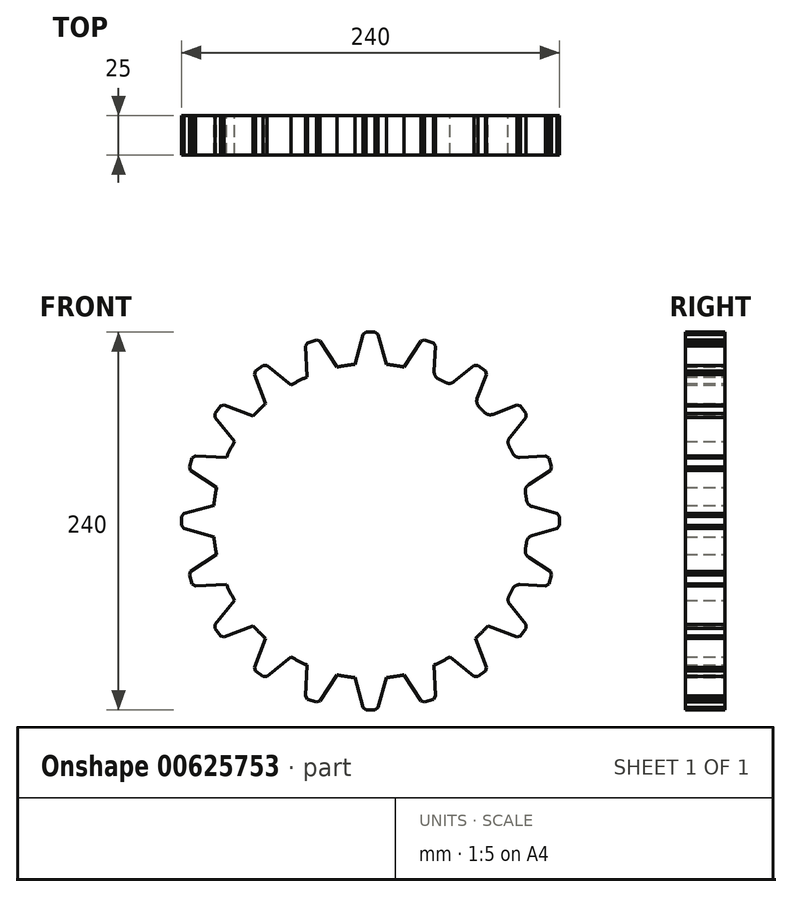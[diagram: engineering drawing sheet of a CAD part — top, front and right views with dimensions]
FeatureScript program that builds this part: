
annotation { "Feature Type Name" : "Feature", "Feature Type Description" : "" }
export const myFeature = defineFeature(function(context is Context, id is Id, definition is map)
    precondition{}
    {
        {
            var Q0;
            Q0=qCreatedBy(makeId("Front.planeOp"),FACE);
            var sketch = newSketch(context, id + "F0", { "sketchPlane" : qUnion([Q0])});
            skArc(sketch, "E0", {"start": v(-40.25, 91.54) * mm, "mid": v(-45.4, 89.1) * mm, "end": v(-50.4, 86.37) * mm});
            skCircle(sketch, "E1", {"center": v(0, 0) * mm, "radius": 120 * mm, "construction": true});
            skLineSegment(sketch, "E2", {"start": v(0, 120) * mm, "end": v(-4.5, 120) * mm});
            skLineSegment(sketch, "E3", {"start": v(0, 120) * mm, "end": v(4.5, 120) * mm});
            skLineSegment(sketch, "E4", {"start": v(4.5, 120) * mm, "end": v(10, 99.5) * mm});
            skLineSegment(sketch, "E5", {"start": v(-4.5, 120) * mm, "end": v(-10, 99.5) * mm});
            skLineSegment(sketch, "E6.1.0", {"start": v(-37.08, 114.13) * mm, "end": v(-32.8, 115.52) * mm});
            skLineSegment(sketch, "E6.1.1", {"start": v(-37.08, 114.13) * mm, "end": v(-41.36, 112.74) * mm});
            skLineSegment(sketch, "E6.1.2", {"start": v(-32.8, 115.52) * mm, "end": v(-21.24, 97.72) * mm});
            skLineSegment(sketch, "E6.1.3", {"start": v(-41.36, 112.74) * mm, "end": v(-40.25, 91.54) * mm});
            skLineSegment(sketch, "E6.2.0", {"start": v(-70.53, 97.08) * mm, "end": v(-66.9, 99.73) * mm});
            skLineSegment(sketch, "E6.2.1", {"start": v(-70.53, 97.08) * mm, "end": v(-74.17, 94.44) * mm});
            skLineSegment(sketch, "E6.2.2", {"start": v(-66.9, 99.73) * mm, "end": v(-50.4, 86.37) * mm});
            skLineSegment(sketch, "E6.2.3", {"start": v(-74.17, 94.44) * mm, "end": v(-66.57, 74.62) * mm});
            skLineSegment(sketch, "E7.3.3.0", {"start": v(-97.08, 70.53) * mm, "end": v(-99.73, 66.9) * mm});
            skLineSegment(sketch, "E7.6.3.0", {"start": v(-94.44, 74.17) * mm, "end": v(-74.62, 66.57) * mm});
            skLineSegment(sketch, "E7.9.3.0", {"start": v(-99.73, 66.9) * mm, "end": v(-86.37, 50.4) * mm});
            skLineSegment(sketch, "E7.11.3.0", {"start": v(-97.08, 70.53) * mm, "end": v(-94.44, 74.17) * mm});
            skLineSegment(sketch, "E7.3.4.0", {"start": v(-114.13, 37.08) * mm, "end": v(-115.52, 32.8) * mm});
            skLineSegment(sketch, "E7.6.4.0", {"start": v(-112.74, 41.36) * mm, "end": v(-91.54, 40.25) * mm});
            skLineSegment(sketch, "E7.9.4.0", {"start": v(-115.52, 32.8) * mm, "end": v(-97.72, 21.24) * mm});
            skLineSegment(sketch, "E7.11.4.0", {"start": v(-114.13, 37.08) * mm, "end": v(-112.74, 41.36) * mm});
            skLineSegment(sketch, "E7.3.5.0", {"start": v(-120, 0) * mm, "end": v(-120, -4.5) * mm});
            skLineSegment(sketch, "E7.6.5.0", {"start": v(-120, 4.5) * mm, "end": v(-99.5, 10) * mm});
            skLineSegment(sketch, "E7.9.5.0", {"start": v(-120, -4.5) * mm, "end": v(-99.5, -10) * mm});
            skLineSegment(sketch, "E7.11.5.0", {"start": v(-120, 0) * mm, "end": v(-120, 4.5) * mm});
            skLineSegment(sketch, "E7.3.6.0", {"start": v(-114.13, -37.08) * mm, "end": v(-112.74, -41.36) * mm});
            skLineSegment(sketch, "E7.6.6.0", {"start": v(-115.52, -32.8) * mm, "end": v(-97.72, -21.24) * mm});
            skLineSegment(sketch, "E7.9.6.0", {"start": v(-112.74, -41.36) * mm, "end": v(-91.54, -40.25) * mm});
            skLineSegment(sketch, "E7.11.6.0", {"start": v(-114.13, -37.08) * mm, "end": v(-115.52, -32.8) * mm});
            skLineSegment(sketch, "E7.3.7.0", {"start": v(-97.08, -70.53) * mm, "end": v(-94.44, -74.17) * mm});
            skLineSegment(sketch, "E7.6.7.0", {"start": v(-99.73, -66.9) * mm, "end": v(-86.37, -50.4) * mm});
            skLineSegment(sketch, "E7.9.7.0", {"start": v(-94.44, -74.17) * mm, "end": v(-74.62, -66.57) * mm});
            skLineSegment(sketch, "E7.11.7.0", {"start": v(-97.08, -70.53) * mm, "end": v(-99.73, -66.9) * mm});
            skLineSegment(sketch, "E7.3.8.0", {"start": v(-70.53, -97.08) * mm, "end": v(-66.9, -99.73) * mm});
            skLineSegment(sketch, "E7.6.8.0", {"start": v(-74.17, -94.44) * mm, "end": v(-66.57, -74.62) * mm});
            skLineSegment(sketch, "E7.9.8.0", {"start": v(-66.9, -99.73) * mm, "end": v(-50.4, -86.37) * mm});
            skLineSegment(sketch, "E7.11.8.0", {"start": v(-70.53, -97.08) * mm, "end": v(-74.17, -94.44) * mm});
            skLineSegment(sketch, "E7.3.9.0", {"start": v(-37.08, -114.13) * mm, "end": v(-32.8, -115.52) * mm});
            skLineSegment(sketch, "E7.6.9.0", {"start": v(-41.36, -112.74) * mm, "end": v(-40.25, -91.54) * mm});
            skLineSegment(sketch, "E7.9.9.0", {"start": v(-32.8, -115.52) * mm, "end": v(-21.24, -97.72) * mm});
            skLineSegment(sketch, "E7.11.9.0", {"start": v(-37.08, -114.13) * mm, "end": v(-41.36, -112.74) * mm});
            skLineSegment(sketch, "E7.3.10.0", {"start": v(0, -120) * mm, "end": v(4.5, -120) * mm});
            skLineSegment(sketch, "E7.6.10.0", {"start": v(-4.5, -120) * mm, "end": v(-10, -99.5) * mm});
            skLineSegment(sketch, "E7.9.10.0", {"start": v(4.5, -120) * mm, "end": v(10, -99.5) * mm});
            skLineSegment(sketch, "E7.11.10.0", {"start": v(0, -120) * mm, "end": v(-4.5, -120) * mm});
            skLineSegment(sketch, "E7.3.11.0", {"start": v(37.08, -114.13) * mm, "end": v(41.36, -112.74) * mm});
            skLineSegment(sketch, "E7.6.11.0", {"start": v(32.8, -115.52) * mm, "end": v(21.24, -97.72) * mm});
            skLineSegment(sketch, "E7.9.11.0", {"start": v(41.36, -112.74) * mm, "end": v(40.25, -91.54) * mm});
            skLineSegment(sketch, "E7.11.11.0", {"start": v(37.08, -114.13) * mm, "end": v(32.8, -115.52) * mm});
            skLineSegment(sketch, "E7.3.12.0", {"start": v(70.53, -97.08) * mm, "end": v(74.17, -94.44) * mm});
            skLineSegment(sketch, "E7.6.12.0", {"start": v(66.9, -99.73) * mm, "end": v(50.4, -86.37) * mm});
            skLineSegment(sketch, "E7.9.12.0", {"start": v(74.17, -94.44) * mm, "end": v(66.57, -74.62) * mm});
            skLineSegment(sketch, "E7.11.12.0", {"start": v(70.53, -97.08) * mm, "end": v(66.9, -99.73) * mm});
            skLineSegment(sketch, "E7.3.13.0", {"start": v(97.08, -70.53) * mm, "end": v(99.73, -66.9) * mm});
            skLineSegment(sketch, "E7.6.13.0", {"start": v(94.44, -74.17) * mm, "end": v(74.62, -66.57) * mm});
            skLineSegment(sketch, "E7.9.13.0", {"start": v(99.73, -66.9) * mm, "end": v(86.37, -50.4) * mm});
            skLineSegment(sketch, "E7.11.13.0", {"start": v(97.08, -70.53) * mm, "end": v(94.44, -74.17) * mm});
            skLineSegment(sketch, "E7.3.14.0", {"start": v(114.13, -37.08) * mm, "end": v(115.52, -32.8) * mm});
            skLineSegment(sketch, "E7.6.14.0", {"start": v(112.74, -41.36) * mm, "end": v(91.54, -40.25) * mm});
            skLineSegment(sketch, "E7.9.14.0", {"start": v(115.52, -32.8) * mm, "end": v(97.72, -21.24) * mm});
            skLineSegment(sketch, "E7.11.14.0", {"start": v(114.13, -37.08) * mm, "end": v(112.74, -41.36) * mm});
            skLineSegment(sketch, "E7.3.15.0", {"start": v(120, 0) * mm, "end": v(120, 4.5) * mm});
            skLineSegment(sketch, "E7.6.15.0", {"start": v(120, -4.5) * mm, "end": v(99.5, -10) * mm});
            skLineSegment(sketch, "E7.9.15.0", {"start": v(120, 4.5) * mm, "end": v(99.5, 10) * mm});
            skLineSegment(sketch, "E7.11.15.0", {"start": v(120, 0) * mm, "end": v(120, -4.5) * mm});
            skLineSegment(sketch, "E7.3.16.0", {"start": v(114.13, 37.08) * mm, "end": v(112.74, 41.36) * mm});
            skLineSegment(sketch, "E7.6.16.0", {"start": v(115.52, 32.8) * mm, "end": v(97.72, 21.24) * mm});
            skLineSegment(sketch, "E7.9.16.0", {"start": v(112.74, 41.36) * mm, "end": v(91.54, 40.25) * mm});
            skLineSegment(sketch, "E7.11.16.0", {"start": v(114.13, 37.08) * mm, "end": v(115.52, 32.8) * mm});
            skLineSegment(sketch, "E7.3.17.0", {"start": v(97.08, 70.53) * mm, "end": v(94.44, 74.17) * mm});
            skLineSegment(sketch, "E7.6.17.0", {"start": v(99.73, 66.9) * mm, "end": v(86.37, 50.4) * mm});
            skLineSegment(sketch, "E7.9.17.0", {"start": v(94.44, 74.17) * mm, "end": v(74.62, 66.57) * mm});
            skLineSegment(sketch, "E7.11.17.0", {"start": v(97.08, 70.53) * mm, "end": v(99.73, 66.9) * mm});
            skLineSegment(sketch, "E7.3.18.0", {"start": v(70.53, 97.08) * mm, "end": v(66.9, 99.73) * mm});
            skLineSegment(sketch, "E7.6.18.0", {"start": v(74.17, 94.44) * mm, "end": v(66.57, 74.62) * mm});
            skLineSegment(sketch, "E7.9.18.0", {"start": v(66.9, 99.73) * mm, "end": v(50.4, 86.37) * mm});
            skLineSegment(sketch, "E7.11.18.0", {"start": v(70.53, 97.08) * mm, "end": v(74.17, 94.44) * mm});
            skLineSegment(sketch, "E7.3.19.0", {"start": v(37.08, 114.13) * mm, "end": v(32.8, 115.52) * mm});
            skLineSegment(sketch, "E7.6.19.0", {"start": v(41.36, 112.74) * mm, "end": v(40.25, 91.54) * mm});
            skLineSegment(sketch, "E7.9.19.0", {"start": v(32.8, 115.52) * mm, "end": v(21.24, 97.72) * mm});
            skLineSegment(sketch, "E7.11.19.0", {"start": v(37.08, 114.13) * mm, "end": v(41.36, 112.74) * mm});
            skArc(sketch, "E8.trimOffspring", {"start": v(-10, 99.5) * mm, "mid": v(-15.64, 98.77) * mm, "end": v(-21.24, 97.72) * mm});
            skArc(sketch, "E9.trimOffspring", {"start": v(21.24, 97.72) * mm, "mid": v(15.64, 98.77) * mm, "end": v(10, 99.5) * mm});
            skArc(sketch, "E10.trimOffspring", {"start": v(50.4, 86.37) * mm, "mid": v(45.4, 89.1) * mm, "end": v(40.25, 91.54) * mm});
            skArc(sketch, "E11.trimOffspring", {"start": v(74.62, 66.57) * mm, "mid": v(70.71, 70.71) * mm, "end": v(66.57, 74.62) * mm});
            skArc(sketch, "E12.trimOffspring", {"start": v(91.54, 40.25) * mm, "mid": v(89.1, 45.4) * mm, "end": v(86.37, 50.4) * mm});
            skArc(sketch, "E13.trimOffspring", {"start": v(99.5, 10) * mm, "mid": v(98.77, 15.64) * mm, "end": v(97.72, 21.24) * mm});
            skArc(sketch, "E14.trimOffspring", {"start": v(97.72, -21.24) * mm, "mid": v(98.77, -15.64) * mm, "end": v(99.5, -10) * mm});
            skArc(sketch, "E15.trimOffspring", {"start": v(86.37, -50.4) * mm, "mid": v(89.1, -45.4) * mm, "end": v(91.54, -40.25) * mm});
            skArc(sketch, "E16.trimOffspring", {"start": v(66.57, -74.62) * mm, "mid": v(70.71, -70.71) * mm, "end": v(74.62, -66.57) * mm});
            skArc(sketch, "E17.trimOffspring", {"start": v(40.25, -91.54) * mm, "mid": v(45.4, -89.1) * mm, "end": v(50.4, -86.37) * mm});
            skArc(sketch, "E18.trimOffspring", {"start": v(10, -99.5) * mm, "mid": v(15.64, -98.77) * mm, "end": v(21.24, -97.72) * mm});
            skArc(sketch, "E19.trimOffspring", {"start": v(-21.24, -97.72) * mm, "mid": v(-15.64, -98.77) * mm, "end": v(-10, -99.5) * mm});
            skArc(sketch, "E20.trimOffspring", {"start": v(-50.4, -86.37) * mm, "mid": v(-45.4, -89.1) * mm, "end": v(-40.25, -91.54) * mm});
            skArc(sketch, "E21.trimOffspring", {"start": v(-74.62, -66.57) * mm, "mid": v(-70.71, -70.71) * mm, "end": v(-66.57, -74.62) * mm});
            skArc(sketch, "E22.trimOffspring", {"start": v(-91.54, -40.25) * mm, "mid": v(-89.1, -45.4) * mm, "end": v(-86.37, -50.4) * mm});
            skArc(sketch, "E23.trimOffspring", {"start": v(-99.5, -10) * mm, "mid": v(-98.77, -15.64) * mm, "end": v(-97.72, -21.24) * mm});
            skArc(sketch, "E24.trimOffspring", {"start": v(-97.72, 21.24) * mm, "mid": v(-98.77, 15.64) * mm, "end": v(-99.5, 10) * mm});
            skArc(sketch, "E25.trimOffspring", {"start": v(-86.37, 50.4) * mm, "mid": v(-89.1, 45.4) * mm, "end": v(-91.54, 40.25) * mm});
            skArc(sketch, "E26.trimOffspring", {"start": v(-66.57, 74.62) * mm, "mid": v(-70.71, 70.71) * mm, "end": v(-74.62, 66.57) * mm});
            skSolve(sketch);
        }
        {
            var Q0;
            Q0=makeQuery(id+"F0.imprint","IMPRINT",FACE,{"disambiguationData":[TD([[makeQuery(id+"F0.imprint","IMPRINT",EDGE,{"derivedFrom":sQuery(id+"F0.wireOp",EDGE,"E0")}),1.0]])]});
            extrude(context, id + "F1", {"entities" : qUnion([Q0]), "endBound" : BoundingType.SYMMETRIC, "depth" : 25 * mm, "offsetDistance" : 25 * mm});
        }
        {
            var Q0;
            Q0=makeQuery(id+"F1.opExtrude","SWEPT_EDGE",EDGE,{"disambiguationData":[OSD([sQuery(id+"F0.wireOp",EDGE,"E7.6.19.0"),sQuery(id+"F0.wireOp",EDGE,"E10.trimOffspring")])]});
            var Q1;
            Q1=makeQuery(id+"F1.opExtrude","SWEPT_EDGE",EDGE,{"disambiguationData":[OSD([sQuery(id+"F0.wireOp",EDGE,"E7.9.18.0"),sQuery(id+"F0.wireOp",EDGE,"E10.trimOffspring")])]});
            fillet(context, id + "F2", {"entities" : qUnion([Q0, Q1]), "radius" : 5 * mm, "tangentPropagation" : true, "allowEdgeOverflow" : false});
        }
        {
            var Q0;
            Q0=makeQuery(id+"F1.opExtrude","SWEPT_EDGE",EDGE,{"disambiguationData":[OSD([sQuery(id+"F0.wireOp",EDGE,"E6.2.0"),sQuery(id+"F0.wireOp",EDGE,"E6.2.2")])]});
            var Q1;
            Q1=makeQuery(id+"F1.opExtrude","SWEPT_EDGE",EDGE,{"disambiguationData":[OSD([sQuery(id+"F0.wireOp",EDGE,"E6.2.1"),sQuery(id+"F0.wireOp",EDGE,"E6.2.3")])]});
            var Q2;
            Q2=makeQuery(id+"F1.opExtrude","SWEPT_EDGE",EDGE,{"disambiguationData":[OSD([sQuery(id+"F0.wireOp",EDGE,"E6.1.0"),sQuery(id+"F0.wireOp",EDGE,"E6.1.2")])]});
            var Q3;
            Q3=makeQuery(id+"F1.opExtrude","SWEPT_EDGE",EDGE,{"disambiguationData":[OSD([sQuery(id+"F0.wireOp",EDGE,"E6.1.1"),sQuery(id+"F0.wireOp",EDGE,"E6.1.3")])]});
            var Q4;
            Q4=makeQuery(id+"F1.opExtrude","SWEPT_EDGE",EDGE,{"disambiguationData":[OSD([sQuery(id+"F0.wireOp",EDGE,"E3"),sQuery(id+"F0.wireOp",EDGE,"E4")])]});
            var Q5;
            Q5=makeQuery(id+"F1.opExtrude","SWEPT_EDGE",EDGE,{"disambiguationData":[OSD([sQuery(id+"F0.wireOp",EDGE,"E2"),sQuery(id+"F0.wireOp",EDGE,"E5")])]});
            var Q6;
            Q6=makeQuery(id+"F1.opExtrude","SWEPT_EDGE",EDGE,{"disambiguationData":[OSD([sQuery(id+"F0.wireOp",EDGE,"E7.6.19.0"),sQuery(id+"F0.wireOp",EDGE,"E7.11.19.0")])]});
            var Q7;
            Q7=makeQuery(id+"F1.opExtrude","SWEPT_EDGE",EDGE,{"disambiguationData":[OSD([sQuery(id+"F0.wireOp",EDGE,"E7.3.19.0"),sQuery(id+"F0.wireOp",EDGE,"E7.9.19.0")])]});
            var Q8;
            Q8=makeQuery(id+"F1.opExtrude","SWEPT_EDGE",EDGE,{"disambiguationData":[OSD([sQuery(id+"F0.wireOp",EDGE,"E7.6.18.0"),sQuery(id+"F0.wireOp",EDGE,"E7.11.18.0")])]});
            var Q9;
            Q9=makeQuery(id+"F1.opExtrude","SWEPT_EDGE",EDGE,{"disambiguationData":[OSD([sQuery(id+"F0.wireOp",EDGE,"E7.3.18.0"),sQuery(id+"F0.wireOp",EDGE,"E7.9.18.0")])]});
            var Q10;
            Q10=makeQuery(id+"F1.opExtrude","SWEPT_EDGE",EDGE,{"disambiguationData":[OSD([sQuery(id+"F0.wireOp",EDGE,"E7.6.17.0"),sQuery(id+"F0.wireOp",EDGE,"E7.11.17.0")])]});
            var Q11;
            Q11=makeQuery(id+"F1.opExtrude","SWEPT_EDGE",EDGE,{"disambiguationData":[OSD([sQuery(id+"F0.wireOp",EDGE,"E7.3.17.0"),sQuery(id+"F0.wireOp",EDGE,"E7.9.17.0")])]});
            var Q12;
            Q12=makeQuery(id+"F1.opExtrude","SWEPT_EDGE",EDGE,{"disambiguationData":[OSD([sQuery(id+"F0.wireOp",EDGE,"E7.6.16.0"),sQuery(id+"F0.wireOp",EDGE,"E7.11.16.0")])]});
            var Q13;
            Q13=makeQuery(id+"F1.opExtrude","SWEPT_EDGE",EDGE,{"disambiguationData":[OSD([sQuery(id+"F0.wireOp",EDGE,"E7.3.16.0"),sQuery(id+"F0.wireOp",EDGE,"E7.9.16.0")])]});
            var Q14;
            Q14=makeQuery(id+"F1.opExtrude","SWEPT_EDGE",EDGE,{"disambiguationData":[OSD([sQuery(id+"F0.wireOp",EDGE,"E7.6.15.0"),sQuery(id+"F0.wireOp",EDGE,"E7.11.15.0")])]});
            var Q15;
            Q15=makeQuery(id+"F1.opExtrude","SWEPT_EDGE",EDGE,{"disambiguationData":[OSD([sQuery(id+"F0.wireOp",EDGE,"E7.3.15.0"),sQuery(id+"F0.wireOp",EDGE,"E7.9.15.0")])]});
            var Q16;
            Q16=makeQuery(id+"F1.opExtrude","SWEPT_EDGE",EDGE,{"disambiguationData":[OSD([sQuery(id+"F0.wireOp",EDGE,"E7.6.14.0"),sQuery(id+"F0.wireOp",EDGE,"E7.11.14.0")])]});
            var Q17;
            Q17=makeQuery(id+"F1.opExtrude","SWEPT_EDGE",EDGE,{"disambiguationData":[OSD([sQuery(id+"F0.wireOp",EDGE,"E7.3.14.0"),sQuery(id+"F0.wireOp",EDGE,"E7.9.14.0")])]});
            var Q18;
            Q18=makeQuery(id+"F1.opExtrude","SWEPT_EDGE",EDGE,{"disambiguationData":[OSD([sQuery(id+"F0.wireOp",EDGE,"E7.6.13.0"),sQuery(id+"F0.wireOp",EDGE,"E7.11.13.0")])]});
            var Q19;
            Q19=makeQuery(id+"F1.opExtrude","SWEPT_EDGE",EDGE,{"disambiguationData":[OSD([sQuery(id+"F0.wireOp",EDGE,"E7.3.13.0"),sQuery(id+"F0.wireOp",EDGE,"E7.9.13.0")])]});
            var Q20;
            Q20=makeQuery(id+"F1.opExtrude","SWEPT_EDGE",EDGE,{"disambiguationData":[OSD([sQuery(id+"F0.wireOp",EDGE,"E7.6.12.0"),sQuery(id+"F0.wireOp",EDGE,"E7.11.12.0")])]});
            var Q21;
            Q21=makeQuery(id+"F1.opExtrude","SWEPT_EDGE",EDGE,{"disambiguationData":[OSD([sQuery(id+"F0.wireOp",EDGE,"E7.3.12.0"),sQuery(id+"F0.wireOp",EDGE,"E7.9.12.0")])]});
            var Q22;
            Q22=makeQuery(id+"F1.opExtrude","SWEPT_EDGE",EDGE,{"disambiguationData":[OSD([sQuery(id+"F0.wireOp",EDGE,"E7.6.11.0"),sQuery(id+"F0.wireOp",EDGE,"E7.11.11.0")])]});
            var Q23;
            Q23=makeQuery(id+"F1.opExtrude","SWEPT_EDGE",EDGE,{"disambiguationData":[OSD([sQuery(id+"F0.wireOp",EDGE,"E7.3.11.0"),sQuery(id+"F0.wireOp",EDGE,"E7.9.11.0")])]});
            var Q24;
            Q24=makeQuery(id+"F1.opExtrude","SWEPT_EDGE",EDGE,{"disambiguationData":[OSD([sQuery(id+"F0.wireOp",EDGE,"E7.6.10.0"),sQuery(id+"F0.wireOp",EDGE,"E7.11.10.0")])]});
            var Q25;
            Q25=makeQuery(id+"F1.opExtrude","SWEPT_EDGE",EDGE,{"disambiguationData":[OSD([sQuery(id+"F0.wireOp",EDGE,"E7.3.10.0"),sQuery(id+"F0.wireOp",EDGE,"E7.9.10.0")])]});
            var Q26;
            Q26=makeQuery(id+"F1.opExtrude","SWEPT_EDGE",EDGE,{"disambiguationData":[OSD([sQuery(id+"F0.wireOp",EDGE,"E7.6.9.0"),sQuery(id+"F0.wireOp",EDGE,"E7.11.9.0")])]});
            var Q27;
            Q27=makeQuery(id+"F1.opExtrude","SWEPT_EDGE",EDGE,{"disambiguationData":[OSD([sQuery(id+"F0.wireOp",EDGE,"E7.3.9.0"),sQuery(id+"F0.wireOp",EDGE,"E7.9.9.0")])]});
            var Q28;
            Q28=makeQuery(id+"F1.opExtrude","SWEPT_EDGE",EDGE,{"disambiguationData":[OSD([sQuery(id+"F0.wireOp",EDGE,"E7.6.8.0"),sQuery(id+"F0.wireOp",EDGE,"E7.11.8.0")])]});
            var Q29;
            Q29=makeQuery(id+"F1.opExtrude","SWEPT_EDGE",EDGE,{"disambiguationData":[OSD([sQuery(id+"F0.wireOp",EDGE,"E7.3.8.0"),sQuery(id+"F0.wireOp",EDGE,"E7.9.8.0")])]});
            var Q30;
            Q30=makeQuery(id+"F1.opExtrude","SWEPT_EDGE",EDGE,{"disambiguationData":[OSD([sQuery(id+"F0.wireOp",EDGE,"E7.6.7.0"),sQuery(id+"F0.wireOp",EDGE,"E7.11.7.0")])]});
            var Q31;
            Q31=makeQuery(id+"F1.opExtrude","SWEPT_EDGE",EDGE,{"disambiguationData":[OSD([sQuery(id+"F0.wireOp",EDGE,"E7.3.7.0"),sQuery(id+"F0.wireOp",EDGE,"E7.9.7.0")])]});
            var Q32;
            Q32=makeQuery(id+"F1.opExtrude","SWEPT_EDGE",EDGE,{"disambiguationData":[OSD([sQuery(id+"F0.wireOp",EDGE,"E7.3.6.0"),sQuery(id+"F0.wireOp",EDGE,"E7.9.6.0")])]});
            var Q33;
            Q33=makeQuery(id+"F1.opExtrude","SWEPT_EDGE",EDGE,{"disambiguationData":[OSD([sQuery(id+"F0.wireOp",EDGE,"E7.6.6.0"),sQuery(id+"F0.wireOp",EDGE,"E7.11.6.0")])]});
            var Q34;
            Q34=makeQuery(id+"F1.opExtrude","SWEPT_EDGE",EDGE,{"disambiguationData":[OSD([sQuery(id+"F0.wireOp",EDGE,"E7.3.5.0"),sQuery(id+"F0.wireOp",EDGE,"E7.9.5.0")])]});
            var Q35;
            Q35=makeQuery(id+"F1.opExtrude","SWEPT_EDGE",EDGE,{"disambiguationData":[OSD([sQuery(id+"F0.wireOp",EDGE,"E7.6.5.0"),sQuery(id+"F0.wireOp",EDGE,"E7.11.5.0")])]});
            var Q36;
            Q36=makeQuery(id+"F1.opExtrude","SWEPT_EDGE",EDGE,{"disambiguationData":[OSD([sQuery(id+"F0.wireOp",EDGE,"E7.3.4.0"),sQuery(id+"F0.wireOp",EDGE,"E7.9.4.0")])]});
            var Q37;
            Q37=makeQuery(id+"F1.opExtrude","SWEPT_EDGE",EDGE,{"disambiguationData":[OSD([sQuery(id+"F0.wireOp",EDGE,"E7.6.4.0"),sQuery(id+"F0.wireOp",EDGE,"E7.11.4.0")])]});
            var Q38;
            Q38=makeQuery(id+"F1.opExtrude","SWEPT_EDGE",EDGE,{"disambiguationData":[OSD([sQuery(id+"F0.wireOp",EDGE,"E7.3.3.0"),sQuery(id+"F0.wireOp",EDGE,"E7.9.3.0")])]});
            var Q39;
            Q39=makeQuery(id+"F1.opExtrude","SWEPT_EDGE",EDGE,{"disambiguationData":[OSD([sQuery(id+"F0.wireOp",EDGE,"E7.6.3.0"),sQuery(id+"F0.wireOp",EDGE,"E7.11.3.0")])]});
            chamfer(context, id + "F3", {"entities" : qUnion([Q0, Q1, Q2, Q3, Q4, Q5, Q6, Q7, Q8, Q9, Q10, Q11, Q12, Q13, Q14, Q15, Q16, Q17, Q18, Q19, Q20, Q21, Q22, Q23, Q24, Q25, Q26, Q27, Q28, Q29, Q30, Q31, Q32, Q33, Q34, Q35, Q36, Q37, Q38, Q39]), "width" : 2 * mm, "tangentPropagation" : true});
        }
        {
            var Q0;
            Q0=makeQuery(id+"F1.opExtrude","SWEPT_EDGE",EDGE,{"disambiguationData":[OSD([sQuery(id+"F0.wireOp",EDGE,"E7.9.17.0"),sQuery(id+"F0.wireOp",EDGE,"E11.trimOffspring")])]});
            var Q1;
            Q1=makeQuery(id+"F1.opExtrude","SWEPT_EDGE",EDGE,{"disambiguationData":[OSD([sQuery(id+"F0.wireOp",EDGE,"E7.6.18.0"),sQuery(id+"F0.wireOp",EDGE,"E11.trimOffspring")])]});
            var Q2;
            Q2=makeQuery(id+"F1.opExtrude","SWEPT_EDGE",EDGE,{"disambiguationData":[OSD([sQuery(id+"F0.wireOp",EDGE,"E7.9.16.0"),sQuery(id+"F0.wireOp",EDGE,"E12.trimOffspring")])]});
            var Q3;
            Q3=makeQuery(id+"F1.opExtrude","SWEPT_EDGE",EDGE,{"disambiguationData":[OSD([sQuery(id+"F0.wireOp",EDGE,"E7.6.17.0"),sQuery(id+"F0.wireOp",EDGE,"E12.trimOffspring")])]});
            var Q4;
            Q4=makeQuery(id+"F1.opExtrude","SWEPT_EDGE",EDGE,{"disambiguationData":[OSD([sQuery(id+"F0.wireOp",EDGE,"E7.6.16.0"),sQuery(id+"F0.wireOp",EDGE,"E13.trimOffspring")])]});
            var Q5;
            Q5=makeQuery(id+"F1.opExtrude","SWEPT_EDGE",EDGE,{"disambiguationData":[OSD([sQuery(id+"F0.wireOp",EDGE,"E7.9.15.0"),sQuery(id+"F0.wireOp",EDGE,"E13.trimOffspring")])]});
            var Q6;
            Q6=makeQuery(id+"F1.opExtrude","SWEPT_EDGE",EDGE,{"disambiguationData":[OSD([sQuery(id+"F0.wireOp",EDGE,"E7.6.15.0"),sQuery(id+"F0.wireOp",EDGE,"E14.trimOffspring")])]});
            var Q7;
            Q7=makeQuery(id+"F1.opExtrude","SWEPT_EDGE",EDGE,{"disambiguationData":[OSD([sQuery(id+"F0.wireOp",EDGE,"E7.9.14.0"),sQuery(id+"F0.wireOp",EDGE,"E14.trimOffspring")])]});
            var Q8;
            Q8=makeQuery(id+"F1.opExtrude","SWEPT_EDGE",EDGE,{"disambiguationData":[OSD([sQuery(id+"F0.wireOp",EDGE,"E7.6.14.0"),sQuery(id+"F0.wireOp",EDGE,"E15.trimOffspring")])]});
            var Q9;
            Q9=makeQuery(id+"F1.opExtrude","SWEPT_EDGE",EDGE,{"disambiguationData":[OSD([sQuery(id+"F0.wireOp",EDGE,"E7.9.13.0"),sQuery(id+"F0.wireOp",EDGE,"E15.trimOffspring")])]});
            fillet(context, id + "F4", {"entities" : qUnion([Q0, Q1, Q2, Q3, Q4, Q5, Q6, Q7, Q8, Q9]), "radius" : 5 * mm, "tangentPropagation" : true, "allowEdgeOverflow" : false});
        }
    });
